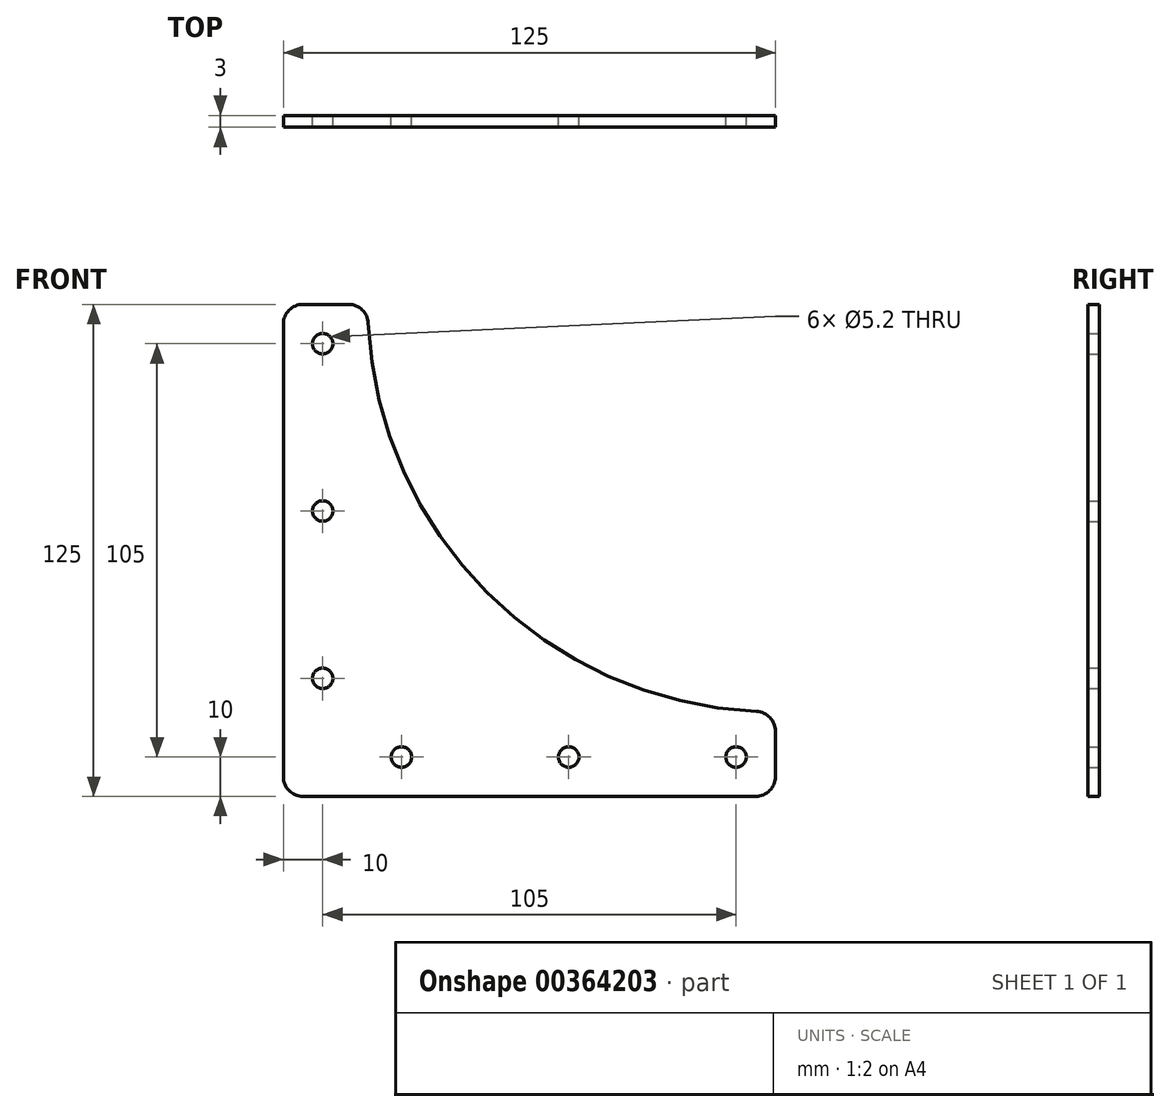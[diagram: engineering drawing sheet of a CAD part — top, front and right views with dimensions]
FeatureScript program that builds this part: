
annotation { "Feature Type Name" : "Feature", "Feature Type Description" : "" }
export const myFeature = defineFeature(function(context is Context, id is Id, definition is map)
    precondition{}
    {
        {
            var Q0;
            Q0=qCreatedBy(makeId("Front.planeOp"),FACE);
            var sketch = newSketch(context, id + "F0", { "sketchPlane" : qUnion([Q0])});
            skLineSegment(sketch, "E0.bottom", {"start": v(57.5, -62.5) * mm, "end": v(-57.5, -62.5) * mm});
            skLineSegment(sketch, "E0.top", {"start": v(-45.93, 62.5) * mm, "end": v(-57.5, 62.5) * mm});
            skLineSegment(sketch, "E0.left", {"start": v(62.5, -57.5) * mm, "end": v(62.5, -45.93) * mm});
            skLineSegment(sketch, "E0.right", {"start": v(-62.5, -57.5) * mm, "end": v(-62.5, 57.5) * mm});
            skPoint(sketch, "E0.middle", {"position": v(0, 0) * mm});
            skPoint(sketch, "E1.orphan", {"position": v(62.5, 62.5) * mm});
            skPoint(sketch, "E2.visualSharp", {"position": v(-62.5, 62.5) * mm});
            skArc(sketch, "E2.filletArc", {"start": v(-57.5, 62.5) * mm, "mid": v(-61.04, 61.04) * mm, "end": v(-62.5, 57.5) * mm});
            skPoint(sketch, "E3.visualSharp", {"position": v(-42.5, 62.5) * mm});
            skPoint(sketch, "E4.visualSharp", {"position": v(62.5, -42.5) * mm});
            skPoint(sketch, "E5.visualSharp", {"position": v(62.5, -62.5) * mm});
            skArc(sketch, "E5.filletArc", {"start": v(57.5, -62.5) * mm, "mid": v(61.04, -61.04) * mm, "end": v(62.5, -57.5) * mm});
            skPoint(sketch, "E6.visualSharp", {"position": v(-62.5, -62.5) * mm});
            skArc(sketch, "E6.filletArc", {"start": v(-62.5, -57.5) * mm, "mid": v(-61.04, -61.04) * mm, "end": v(-57.5, -62.5) * mm});
            skLineSegment(sketch, "E7", {"start": v(-52.5, 52.5) * mm, "end": v(-52.5, -32.5) * mm, "construction": true});
            skCircle(sketch, "E8", {"center": v(-52.5, 52.5) * mm, "radius": 2.6 * mm});
            skCircle(sketch, "E9", {"center": v(52.5, -52.5) * mm, "radius": 2.6 * mm});
            skCircle(sketch, "E10", {"center": v(-52.5, -32.5) * mm, "radius": 2.6 * mm});
            skCircle(sketch, "E11", {"center": v(-32.5, -52.5) * mm, "radius": 2.6 * mm});
            skLineSegment(sketch, "E12.trimOffspring", {"start": v(-32.5, -52.5) * mm, "end": v(52.5, -52.5) * mm, "construction": true});
            skCircle(sketch, "E13", {"center": v(-52.5, 10) * mm, "radius": 2.6 * mm});
            skCircle(sketch, "E14", {"center": v(10, -52.5) * mm, "radius": 2.6 * mm});
            skArc(sketch, "E15", {"start": v(-40.94, 57.73) * mm, "mid": v(-10.72, -10.72) * mm, "end": v(57.73, -40.94) * mm});
            skArc(sketch, "E16.filletArc", {"start": v(62.5, -45.93) * mm, "mid": v(61.12, -42.48) * mm, "end": v(57.73, -40.94) * mm});
            skArc(sketch, "E17.filletArc", {"start": v(-40.94, 57.73) * mm, "mid": v(-42.48, 61.12) * mm, "end": v(-45.93, 62.5) * mm});
            skSolve(sketch);
        }
        {
            var Q0;
            Q0=makeQuery(id+"F0.imprint","IMPRINT",FACE,{"disambiguationData":[TD([[makeQuery(id+"F0.imprint","IMPRINT",EDGE,{"derivedFrom":sQuery(id+"F0.wireOp",EDGE,"E0.bottom")}),-1.0]])]});
            extrude(context, id + "F1", {"entities" : qUnion([Q0]), "depth" : 3 * mm, "offsetDistance" : 25 * mm});
        }
    });
